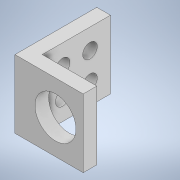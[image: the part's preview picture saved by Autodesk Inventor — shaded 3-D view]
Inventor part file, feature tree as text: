
AUTODESK INVENTOR PART (.ipt)
format: ipt  version: 2022.2 (Build 262287010, 287A)  size: 140,800 bytes
history: native  units: in
note: dims shown in document units (in); Inventor stores cm internally (conversion verified against a paired STEP export)
features: sketch x4, extrude x3, hole x1
ambient origin geometry x8: Origin, YZ Plane, XZ Plane, XY Plane, X Axis, Y Axis, Z Axis, Center Point
bodies: Solid1 (feature_tree)
feature tree (8):
  extrude  "Extrusion1"  Depth=1.5in
  extrude  "Extrusion2"  Depth=0.25in
  extrude  "Extrusion3"  Depth=1.0in
  hole  "Hole1"  [1 undecoded]
  sketch  "Sketch1"  dims[d0=1.25in d1=1.5in]
  sketch  "Sketch2"  dims[d2=0.25in d3=0.0in d4=0.25in]
  sketch  "Sketch3"  dims[d5=1.0in d6=0.0in d7=0.7421in]
  sketch  "Sketch4"  dims[d8=0.75in d9=0.0in d10=0.0in d11=0.0in d12=0.375in d13=0.375in d14=0.375in d15=0.375in d16=0.266in d17=0.75in d18=0.625in d19=0.19in d20=0.5635in d21=0.31in d22=0.0in]
note: 1 required parameter value undecoded (feature->parameter linkage not recoverable at this tier; creation-order binding heuristic only, values carry confidence <= 0.55)
